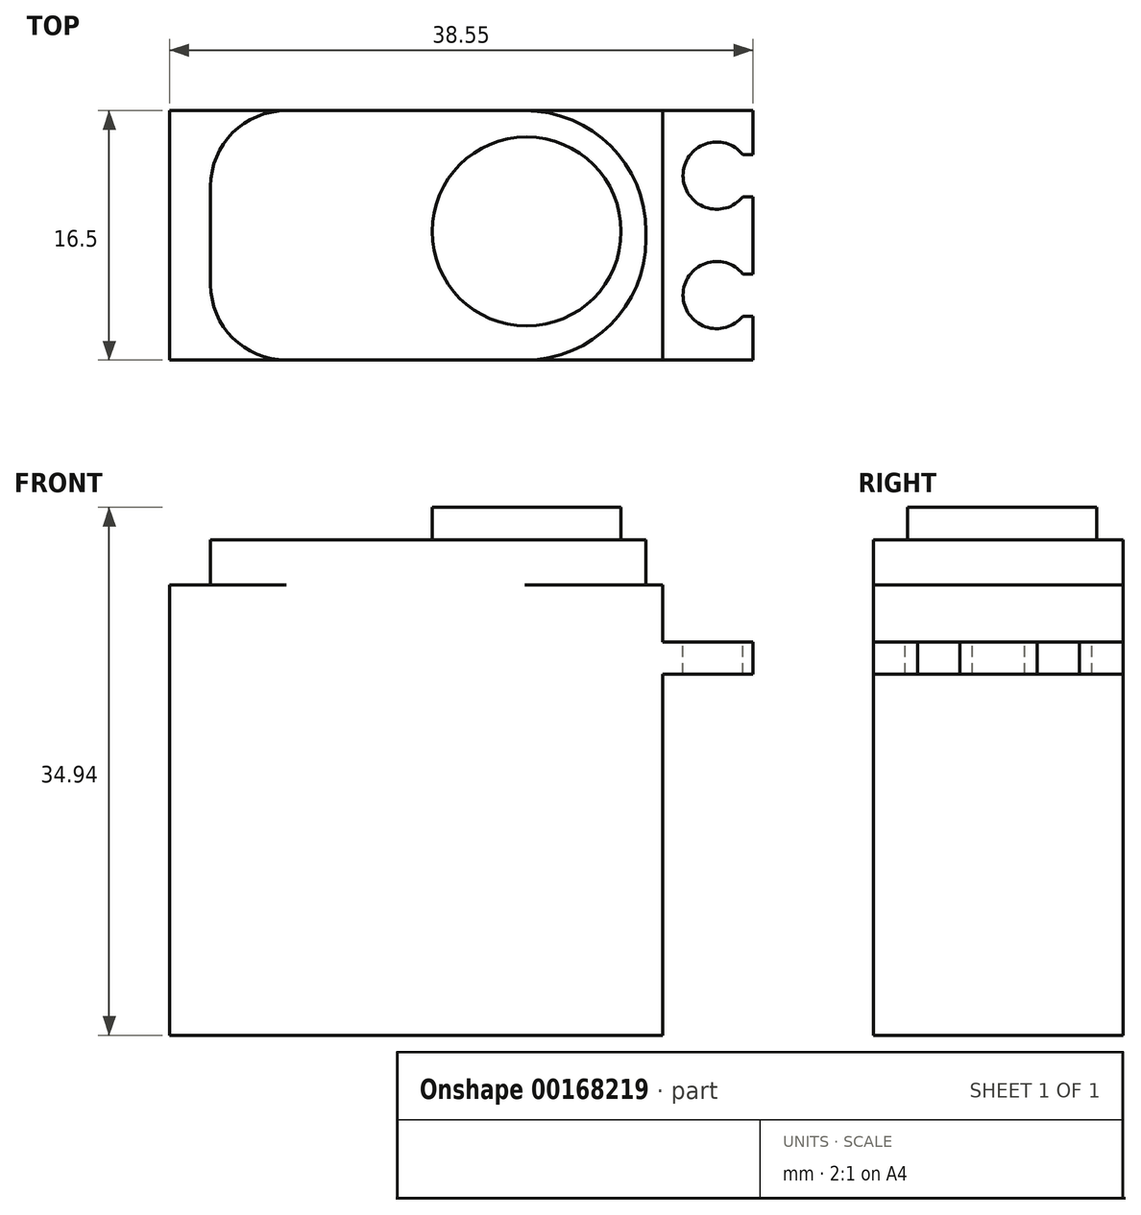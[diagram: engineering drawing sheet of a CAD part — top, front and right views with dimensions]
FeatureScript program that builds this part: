
annotation { "Feature Type Name" : "Feature", "Feature Type Description" : "" }
export const myFeature = defineFeature(function(context is Context, id is Id, definition is map)
    precondition{}
    {
        {
            var Q0;
            Q0=qCreatedBy(makeId("Front.planeOp"),FACE);
            var sketch = newSketch(context, id + "F0", { "sketchPlane" : qUnion([Q0])});
            skLineSegment(sketch, "E0.bottom", {"start": v(16.3, 14.9) * mm, "end": v(-16.3, 14.9) * mm});
            skLineSegment(sketch, "E0.top", {"start": v(16.3, -14.9) * mm, "end": v(-16.3, -14.9) * mm});
            skLineSegment(sketch, "E0.left", {"start": v(16.3, 14.9) * mm, "end": v(16.3, -14.9) * mm});
            skLineSegment(sketch, "E0.right", {"start": v(-16.3, 14.9) * mm, "end": v(-16.3, -14.9) * mm});
            skPoint(sketch, "E0.middle", {"position": v(0, 0) * mm});
            skSolve(sketch);
        }
        {
            var Q0;
            Q0 = qSketchRegion(id + "F0", true);
            extrude(context, id + "F1", {"entities" : qUnion([Q0]), "depth" : 16.5 * mm, "offsetDistance" : 25 * mm});
        }
        {
            var Q0;
            Q0=makeQuery(id+"F1.opExtrude","SWEPT_FACE",FACE,{"disambiguationData":[OSD([sQuery(id+"F0.wireOp",EDGE,"E0.bottom")])]});
            var sketch = newSketch(context, id + "F2", { "sketchPlane" : qUnion([Q0])});
            skLineSegment(sketch, "E1.bottom", {"start": v(-13.6, 0) * mm, "end": v(15.2, 0) * mm});
            skLineSegment(sketch, "E1.top", {"start": v(-13.6, -16.5) * mm, "end": v(15.2, -16.5) * mm});
            skLineSegment(sketch, "E1.left", {"start": v(-13.6, 0) * mm, "end": v(-13.6, -16.5) * mm});
            skLineSegment(sketch, "E1.right", {"start": v(15.2, 0) * mm, "end": v(15.2, -16.5) * mm});
            skSolve(sketch);
        }
        {
            var Q0;
            Q0 = qSketchRegion(id + "F2", true);
            extrude(context, id + "F3", {"entities" : qUnion([Q0]), "operationType" : NewBodyOperationType.ADD, "depth" : 3 * mm, "offsetDistance" : 25 * mm});
        }
        {
            var Q0;
            Q0=makeQuery(id+"F3.opExtrude","SWEPT_EDGE",EDGE,{"disambiguationData":[OSD([sQuery(id+"F0.wireOp",EDGE,"E0.bottom"),sQuery(id+"F2.wireOp",EDGE,"E1.top"),sQuery(id+"F2.wireOp",EDGE,"E1.right")])]});
            var Q1;
            Q1=makeQuery(id+"F3.opExtrude","SWEPT_EDGE",EDGE,{"disambiguationData":[OSD([sQuery(id+"F0.wireOp",EDGE,"E0.bottom"),sQuery(id+"F2.wireOp",EDGE,"E1.bottom"),sQuery(id+"F2.wireOp",EDGE,"E1.right")])]});
            fillet(context, id + "F4", {"entities" : qUnion([Q0, Q1]), "radius" : 8 * mm, "tangentPropagation" : true, "allowEdgeOverflow" : false});
        }
        {
            var Q0;
            Q0=makeQuery(id+"F3.opExtrude","SWEPT_EDGE",EDGE,{"disambiguationData":[OSD([sQuery(id+"F0.wireOp",EDGE,"E0.bottom"),sQuery(id+"F2.wireOp",EDGE,"E1.top"),sQuery(id+"F2.wireOp",EDGE,"E1.left")])]});
            var Q1;
            Q1=makeQuery(id+"F3.opExtrude","SWEPT_EDGE",EDGE,{"disambiguationData":[OSD([sQuery(id+"F0.wireOp",EDGE,"E0.bottom"),sQuery(id+"F2.wireOp",EDGE,"E1.bottom"),sQuery(id+"F2.wireOp",EDGE,"E1.left")])]});
            fillet(context, id + "F5", {"entities" : qUnion([Q0, Q1]), "radius" : 5 * mm, "tangentPropagation" : true, "allowEdgeOverflow" : false});
        }
        {
            var Q0;
            Q0=makeQuery(id+"F3.opExtrude","CAP_FACE",FACE,{"disambiguationData":[OSD([sQuery(id+"F2.wireOp",EDGE,"E1.bottom"),sQuery(id+"F2.wireOp",EDGE,"E1.top"),sQuery(id+"F2.wireOp",EDGE,"E1.left"),sQuery(id+"F2.wireOp",EDGE,"E1.right")])],"isStart":false});
            var sketch = newSketch(context, id + "F6", { "sketchPlane" : qUnion([Q0])});
            skCircle(sketch, "E2", {"center": v(7.3, -8) * mm, "radius": 6.25 * mm});
            skLineSegment(sketch, "E3", {"start": v(15.2, -8) * mm, "end": v(-13.6, -8) * mm, "construction": true});
            skSolve(sketch);
        }
        {
            var Q0;
            Q0 = qSketchRegion(id + "F6", true);
            extrude(context, id + "F7", {"entities" : qUnion([Q0]), "operationType" : NewBodyOperationType.ADD, "depth" : 2.14 * mm, "offsetDistance" : 25 * mm});
        }
        {
            var Q0;
            Q0=makeQuery(id+"F1.opExtrude","SWEPT_FACE",FACE,{"disambiguationData":[OSD([sQuery(id+"F0.wireOp",EDGE,"E0.left")])]});
            var sketch = newSketch(context, id + "F8", { "sketchPlane" : qUnion([Q0])});
            skLineSegment(sketch, "E4.bottom", {"start": v(-16.5, 11.12) * mm, "end": v(0, 11.12) * mm});
            skLineSegment(sketch, "E4.top", {"start": v(-16.5, 8.98) * mm, "end": v(0, 8.98) * mm});
            skLineSegment(sketch, "E4.left", {"start": v(-16.5, 11.12) * mm, "end": v(-16.5, 8.98) * mm});
            skLineSegment(sketch, "E4.right", {"start": v(0, 11.12) * mm, "end": v(0, 8.98) * mm});
            skSolve(sketch);
        }
        {
            var Q0;
            Q0 = qSketchRegion(id + "F8", true);
            extrude(context, id + "F9", {"entities" : qUnion([Q0]), "operationType" : NewBodyOperationType.ADD, "depth" : 5.95 * mm, "offsetDistance" : 25 * mm});
        }
        {
            var Q0;
            Q0=makeQuery(id+"F9.opExtrude","SWEPT_FACE",FACE,{"disambiguationData":[OSD([sQuery(id+"F8.wireOp",EDGE,"E4.bottom")])]});
            var sketch = newSketch(context, id + "F10", { "sketchPlane" : qUnion([Q0])});
            skCircle(sketch, "E5", {"center": v(19.87, -4.3) * mm, "radius": 2.23 * mm});
            skLineSegment(sketch, "E6", {"start": v(16.3, -8.25) * mm, "end": v(22.25, -8.25) * mm, "construction": true});
            skCircle(sketch, "E7.MirrorC", {"center": v(19.87, -12.2) * mm, "radius": 2.23 * mm});
            skLineSegment(sketch, "E8.bottom", {"start": v(22.25, -2.9) * mm, "end": v(21.6, -2.9) * mm});
            skLineSegment(sketch, "E8.top", {"start": v(22.25, -5.7) * mm, "end": v(21.6, -5.7) * mm});
            skLineSegment(sketch, "E8.left", {"start": v(22.25, -2.9) * mm, "end": v(22.25, -5.7) * mm});
            skLineSegment(sketch, "E8.right", {"start": v(21.6, -2.9) * mm, "end": v(21.6, -5.7) * mm});
            skLineSegment(sketch, "E9.MirrorCS", {"start": v(22.25, -10.8) * mm, "end": v(21.6, -10.8) * mm});
            skLineSegment(sketch, "E10.MirrorCS", {"start": v(21.6, -13.6) * mm, "end": v(21.6, -10.8) * mm});
            skLineSegment(sketch, "E11.MirrorCS", {"start": v(22.25, -13.6) * mm, "end": v(21.6, -13.6) * mm});
            skLineSegment(sketch, "E12.MirrorCS", {"start": v(22.25, -13.6) * mm, "end": v(22.25, -10.8) * mm});
            skSolve(sketch);
        }
        {
            var Q0;
            Q0 = qSketchRegion(id + "F10", true);
            extrude(context, id + "F11", {"entities" : qUnion([Q0]), "operationType" : NewBodyOperationType.REMOVE, "endBound" : BoundingType.THROUGH_ALL, "oppositeDirection" : true, "depth" : 25 * mm, "offsetDistance" : 25 * mm});
        }
    });
